# Revit family: Air_Conditioner-Packaged-Friedrich-Vert_I_Pak-Heat_Pump
name_source: partatom
category: Mechanical Equipment
revit_build: Autodesk Revit 2015 (Build: 20140606_1530(x64)
units: mm (PartAtom-declared; Revit-internal decimal feet)

## types (1)
- (See Type Catalog)
    04 CSI = 23 81 00
    95 CSI = 15730
    Air Supply Radius = 5.00"
    Amperage = 4 A
    Assembly Code = D3050
    COP = 3
    Condensate Drain Flow = 0 GPM
    Connector Description = Supply Air Outlet Connection
    Cooling Nominal Input Power = 0 VA
    Depth = 23.00"
    Description = Single Package Vertical Air Conditioner
    Drain Radius = 0.38"
    EER Rating = 9.8
    Electric Heat Wattage = 0 W
    Frame Material = Metal - Friedrich - Stainless Steel
    Frequency = 60 Hz
    Full Load Current = 4 A
    Heat Pump Current = 0 A
    Heater Size = 2.5/3.4/5.0
    Heating Nominal Input Power = 0 VA
    Height = 32.00"
    Indoor Motor Amperage = 1 A
    Indoor Motor HP = 1/4
    Installation and Maintenance URL = http://friedrich.com
    Load Classification = HVAC
    Locked Rotor Current = 22 A
    Manufacturer = Friedrich
    Max ESP = 0.30"
    Model = VEH Heat Pump Models
    Number of Poles = 1
    Outdoor Motor Amperage = 0 A
    Phase = 1
    Power Factor = 1
    Product Line = Vert-I-Pak
    Product Page URL = http://friedrich.com
    Product data url = https://bimobject.com
    R 410A Charge Capacity = 34
    Refrigerant Charge = 2.13 lb
    Sensible Heat Ratio = 0.74
    Subcategory = Commercial Air Conditioning
    Submittal URL = http://friedrich.com
    Total Cooling Capacity = 9400.0 Btu/h
    Total Heating Capacity = 0.0 Btu/h
    URL = http://friedrich.com
    Vent Airflow = 60 CFM
    Voltage = 230 V
    Voltage Range = 253-198 V
    Warranty URL = http://friedrich.com
    Weight = 114.00 lb
    Width = 23.00"
    ecoScorecard Product Page = http://ecoscorecard.com

## geometry (parser evidence)
native form markers: Blend x6, Sweep x4
no freeform markers — native parametric forms only
